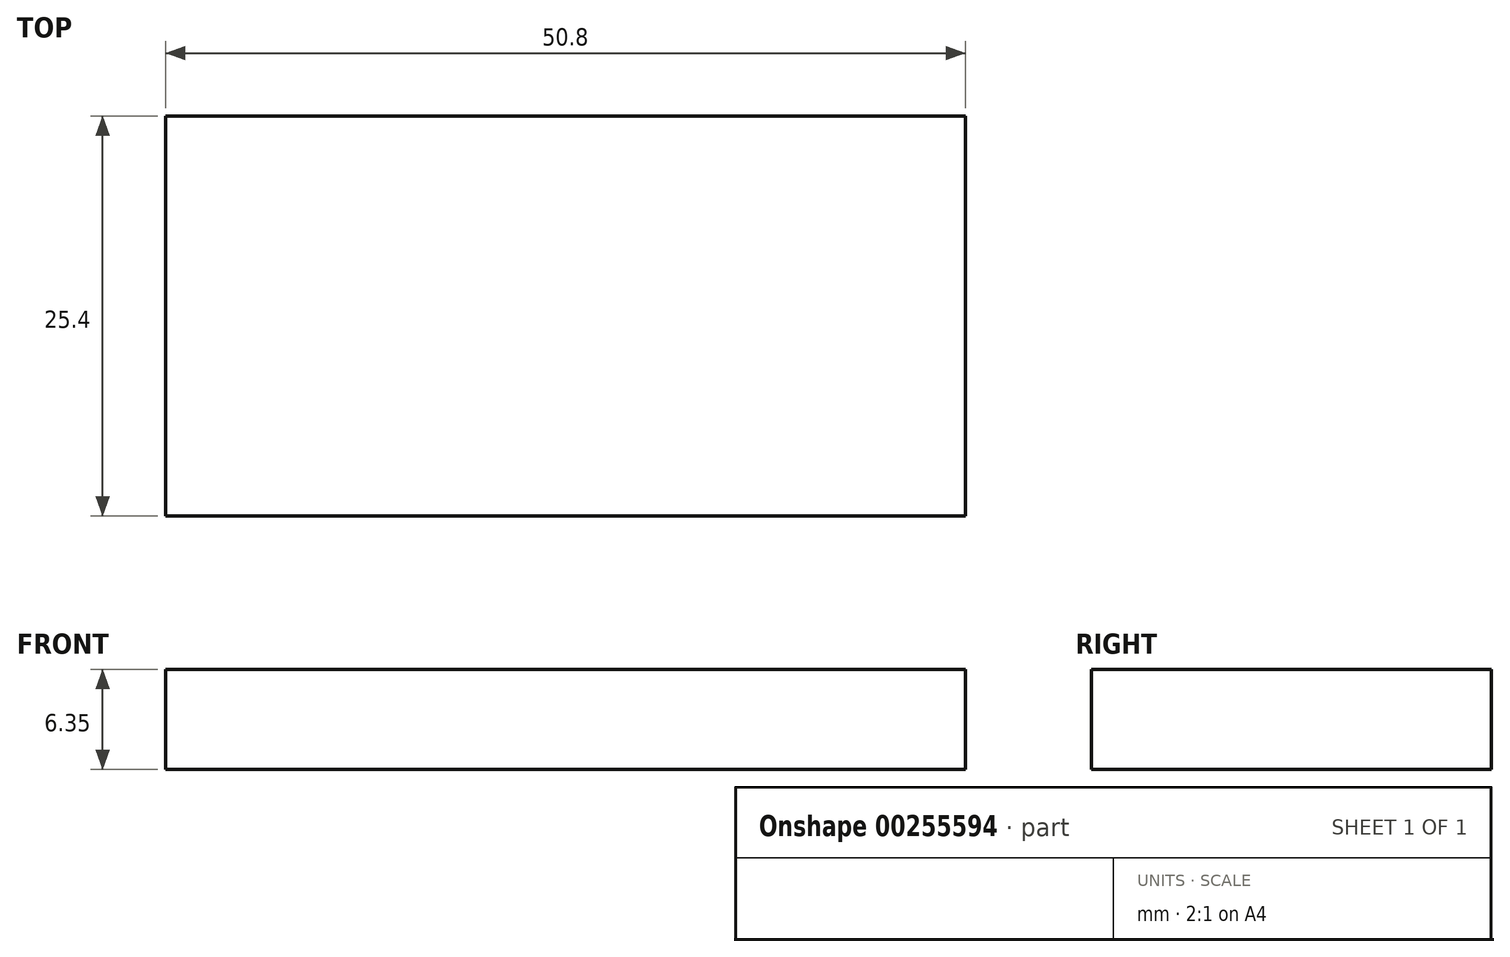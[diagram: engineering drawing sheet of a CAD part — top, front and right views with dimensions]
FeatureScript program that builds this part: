
annotation { "Feature Type Name" : "Feature", "Feature Type Description" : "" }
export const myFeature = defineFeature(function(context is Context, id is Id, definition is map)
    precondition{}
    {
        {
            var Q0;
            Q0=qCreatedBy(makeId("Top.planeOp"),FACE);
            var sketch = newSketch(context, id + "F0", { "sketchPlane" : qUnion([Q0])});
            skLineSegment(sketch, "E0.bottom", {"start": v(0, 0) * mm, "end": v(-50.8, 0) * mm});
            skLineSegment(sketch, "E0.top", {"start": v(0, 25.4) * mm, "end": v(-50.8, 25.4) * mm});
            skLineSegment(sketch, "E0.left", {"start": v(0, 0) * mm, "end": v(0, 25.4) * mm});
            skLineSegment(sketch, "E0.right", {"start": v(-50.8, 0) * mm, "end": v(-50.8, 25.4) * mm});
            skSolve(sketch);
        }
        {
            var Q0;
            Q0 = qSketchRegion(id + "F0", true);
            extrude(context, id + "F1", {"entities" : qUnion([Q0]), "depth" : 6.35 * mm});
        }
    });
